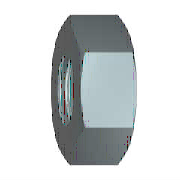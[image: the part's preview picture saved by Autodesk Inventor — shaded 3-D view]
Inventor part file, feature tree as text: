
AUTODESK INVENTOR PART (.ipt)
format: ipt  version: 2023 (Build 270158000, 158)  size: 163,328 bytes
history: native  units: mm (DEFAULTED — no unit token found)
features: sketch x3, other x2, extrude x1, hole x1, plane x1
ambient origin geometry x7: Origin, YZ Plane, XZ Plane, X Axis, Y Axis, Z Axis, Center Point
bodies: Solid1 (feature_tree)
feature tree (8):
  extrude  "Базовый элемент"  Depth=15.011107mm
  other  "Фаска1"
  hole  "Резьба"  [1 undecoded]
  other  "Work Axis1"
  plane  "Work Plane1"
  sketch  "Эскиз1"
  sketch  "Эскиз2"
  sketch  "Эскиз3"
note: 1 required parameter value undecoded (feature->parameter linkage not recoverable at this tier; creation-order binding heuristic only, values carry confidence <= 0.55)
